# Revit family: Faucet-Wall_Mount-Lavatory-KOHLER-Composed-K-73061IN_1
name_source: partatom
category: Plumbing Fixtures
units: mm (PartAtom-declared; Revit-internal decimal feet)

## family parameters
Cut with Voids When Loaded = No
Host = Face
OmniClass Number = 23.31.11.00
Part Type = Normal
Room Calculation Point = No
Round Connector Dimension = Use Diameter
Shared = No

## types (2) — shared parameters
ADA Compliant = No
Assembly Code = D2010
CW Connection = Yes
Cold Water Inlet = Cold Water Inlet
Date Modified = 12/11/2024
Default Elevation = 36"
Drain Included = No
Flow Rate = 2 GPM
HW Connection = Yes
Height = 3 1/4"
Hot Water Inlet = Hot Water Inlet
Length = 6 5/8"
Manufacturer = Kohler Co.
Master Format 2014 = 22 41 39
Master Format 2014 Name = Residential Faucets, Supplies, and Trim
Material = Brass Construction
Pressure = 45.00 psi
Product Name = Composed
Spout Reach = 6 5/8"
URL = https://www.kohler.co.in
Vent Connection = No
Waste Connection = No
Waste Water Outlet = Waste Water Outlet
WaterSense Certified = No
Width = 9 1/16"

## per-type parameters (varying)
| type | Description | Finish | Model | Product Page URL | Type |
| CP-Polished Chrome | Wall Mount Lavatory Faucet | Kohler-Metal-CP-Polished_Chrome | K-73061IN-4ND-CP | https://www.kohler.co.in | 1 |
| BRD-Brushed Rose Gold | MC SINGLE HANDLE WALL MOUNT LAVATORY FAUCET | KOHLER-Metal-BRD-Brushed_Rose_Gold | K-73061IN-7-BRD |  | 2 |

## geometry (parser evidence)
native form markers: Sweep x5
no freeform markers — native parametric forms only
